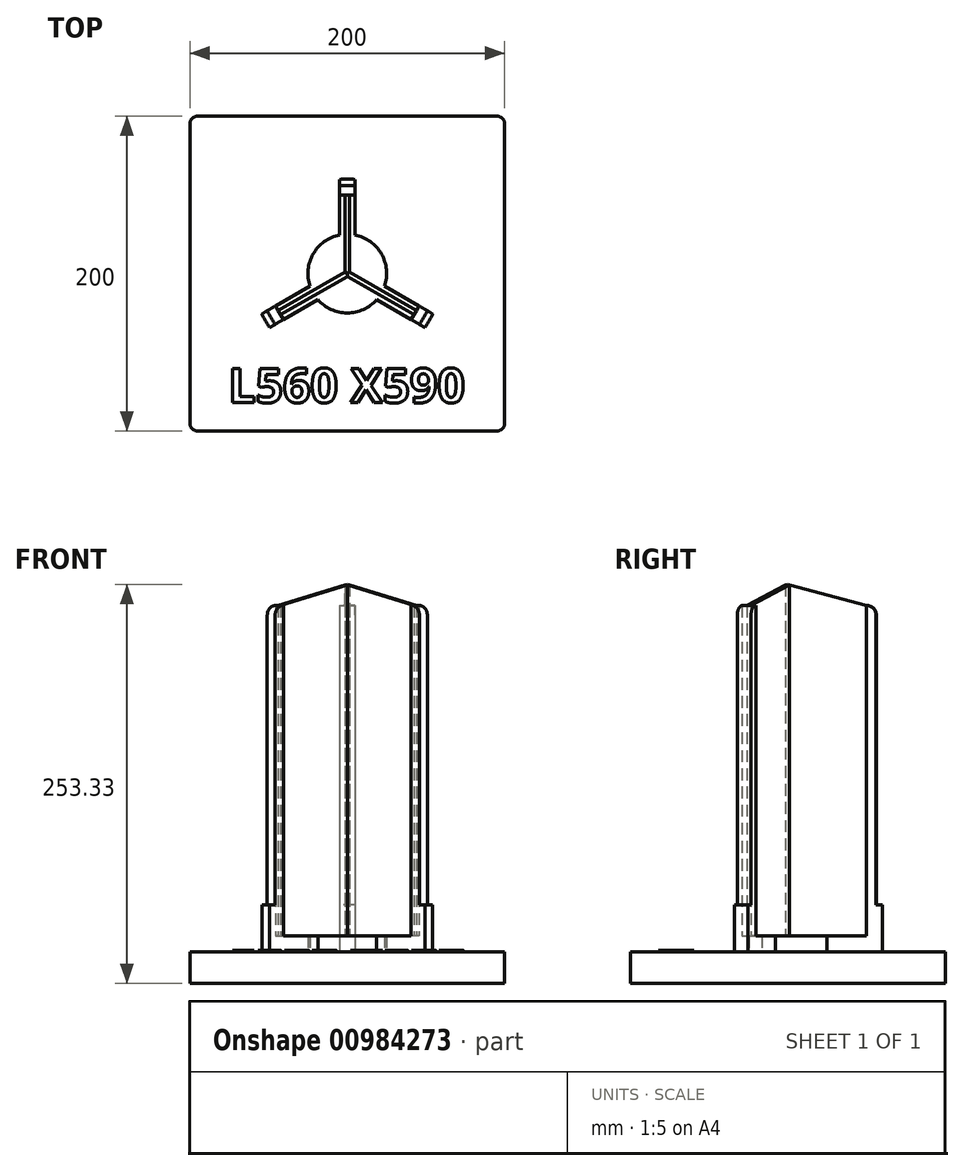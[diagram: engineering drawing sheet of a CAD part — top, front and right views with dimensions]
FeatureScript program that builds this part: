
annotation { "Feature Type Name" : "Feature", "Feature Type Description" : "" }
export const myFeature = defineFeature(function(context is Context, id is Id, definition is map)
    precondition{}
    {
        {
            var Q0;
            Q0=qCreatedBy(makeId("Top.planeOp"),FACE);
            var sketch = newSketch(context, id + "F0", { "sketchPlane" : qUnion([Q0])});
            skCircle(sketch, "E0", {"center": v(0, 0) * mm, "radius": 60 * mm});
            skCircle(sketch, "E1", {"center": v(0, 0) * mm, "radius": 56 * mm});
            skCircle(sketch, "E2", {"center": v(0, 0) * mm, "radius": 25 * mm});
            skLineSegment(sketch, "E3", {"start": v(-1.5, 55.98) * mm, "end": v(1.5, 55.98) * mm, "construction": true});
            skLineSegment(sketch, "E4", {"start": v(-5, 59.8) * mm, "end": v(5, 59.8) * mm, "construction": true});
            skCircle(sketch, "E5", {"center": v(0, 0) * mm, "radius": 1.5 * mm, "construction": true});
            skLineSegment(sketch, "E6", {"start": v(-1.5, 55.98) * mm, "end": v(-1.5, 0) * mm});
            skLineSegment(sketch, "E7", {"start": v(1.5, 55.98) * mm, "end": v(1.5, 0) * mm});
            skLineSegment(sketch, "E8", {"start": v(-5, 59.8) * mm, "end": v(-5, 55.78) * mm});
            skLineSegment(sketch, "E9", {"start": v(5, 59.8) * mm, "end": v(5, 55.78) * mm});
            skLineSegment(sketch, "E10", {"start": v(-1.5, 24.95) * mm, "end": v(-22.36, -11.18) * mm, "construction": true});
            skCircle(sketch, "E11", {"center": v(-11.93, 6.89) * mm, "radius": 3.5 * mm});
            skCircle(sketch, "E12", {"center": v(-11.93, 6.89) * mm, "radius": 1.75 * mm});
            skCircle(sketch, "E13.1.0", {"center": v(0, -13.78) * mm, "radius": 1.75 * mm});
            skCircle(sketch, "E13.1.1", {"center": v(0, -13.78) * mm, "radius": 3.5 * mm});
            skCircle(sketch, "E13.2.0", {"center": v(11.93, 6.89) * mm, "radius": 1.75 * mm});
            skCircle(sketch, "E13.2.1", {"center": v(11.93, 6.89) * mm, "radius": 3.5 * mm});
            skLineSegment(sketch, "E14", {"start": v(-5, 55.78) * mm, "end": v(-5, 24.5) * mm});
            skLineSegment(sketch, "E15", {"start": v(5, 55.78) * mm, "end": v(5, 24.5) * mm});
            skCircle(sketch, "E16", {"center": v(0, 0) * mm, "radius": 50 * mm, "construction": true});
            skLineSegment(sketch, "E17", {"start": v(-5, 49.75) * mm, "end": v(5, 49.75) * mm});
            skLineSegment(sketch, "E18.1.0", {"start": v(-47.73, -29.29) * mm, "end": v(0.75, -1.3) * mm});
            skLineSegment(sketch, "E18.1.1", {"start": v(-49.23, -26.7) * mm, "end": v(-0.75, 1.3) * mm});
            skLineSegment(sketch, "E18.1.2", {"start": v(-45.8, -32.22) * mm, "end": v(-18.71, -16.58) * mm});
            skLineSegment(sketch, "E18.1.3", {"start": v(-50.8, -23.56) * mm, "end": v(-23.71, -7.92) * mm});
            skLineSegment(sketch, "E18.1.4", {"start": v(-49.28, -34.23) * mm, "end": v(-45.8, -32.22) * mm});
            skLineSegment(sketch, "E18.1.5", {"start": v(-54.28, -25.57) * mm, "end": v(-50.8, -23.56) * mm});
            skLineSegment(sketch, "E18.1.6", {"start": v(-49.28, -34.23) * mm, "end": v(-54.28, -25.57) * mm, "construction": true});
            skLineSegment(sketch, "E18.1.7", {"start": v(-47.73, -29.29) * mm, "end": v(-49.23, -26.7) * mm, "construction": true});
            skLineSegment(sketch, "E18.1.8", {"start": v(-40.58, -29.2) * mm, "end": v(-45.58, -20.54) * mm});
            skLineSegment(sketch, "E18.2.0", {"start": v(49.23, -26.7) * mm, "end": v(0.75, 1.3) * mm});
            skLineSegment(sketch, "E18.2.1", {"start": v(47.73, -29.29) * mm, "end": v(-0.75, -1.3) * mm});
            skLineSegment(sketch, "E18.2.2", {"start": v(50.8, -23.56) * mm, "end": v(23.71, -7.92) * mm});
            skLineSegment(sketch, "E18.2.3", {"start": v(45.8, -32.22) * mm, "end": v(18.71, -16.58) * mm});
            skLineSegment(sketch, "E18.2.4", {"start": v(54.28, -25.57) * mm, "end": v(50.8, -23.56) * mm});
            skLineSegment(sketch, "E18.2.5", {"start": v(49.28, -34.23) * mm, "end": v(45.8, -32.22) * mm});
            skLineSegment(sketch, "E18.2.6", {"start": v(54.28, -25.57) * mm, "end": v(49.28, -34.23) * mm, "construction": true});
            skLineSegment(sketch, "E18.2.7", {"start": v(49.23, -26.7) * mm, "end": v(47.73, -29.29) * mm, "construction": true});
            skLineSegment(sketch, "E18.2.8", {"start": v(45.58, -20.54) * mm, "end": v(40.58, -29.2) * mm});
            skText(sketch, "E19", { "text": "L560 X590", "fontName": "OpenSans-Bold.ttf"});
            const initialGuessF0  = {"E19": [-0.07556, -0.082, 1, 0, 0.022]};
            skSetInitialGuess(sketch, initialGuessF0);
            skSolve(sketch);
        }
        {
            var Q0;
            {var subQ0=sQuery(id+"F0.wireOp",EDGE,"E2");var subQ1=sQuery(id+"F0.wireOp",EDGE,"Qz9RoNIK-bmAM-g4SH-EP3c-7Fqs6VSRPzqB.left");var subQ2=makeQuery(id+"F0.imprint","INTERSECT",VERTEX,{"disambiguationData":[OD(0.0)],"derivedFrom":[subQ1,subQ0]});Q0=makeQuery(id+"F0.imprint","IMPRINT",FACE,{"disambiguationData":[TD([[makeQuery(id+"F0.imprint","IMPRINT",EDGE,{"disambiguationData":[TD([[subQ2,-1.0]])],"derivedFrom":subQ1}),1.0]])]});}
            var Q1;
            {var subQ0=sQuery(id+"F0.wireOp",EDGE,"E2");var subQ1=sQuery(id+"F0.wireOp",EDGE,"Qz9RoNIK-bmAM-g4SH-EP3c-7Fqs6VSRPzqB.left");var subQ2=makeQuery(id+"F0.imprint","INTERSECT",VERTEX,{"disambiguationData":[OD(0.0)],"derivedFrom":[subQ1,subQ0]});Q1=makeQuery(id+"F0.imprint","IMPRINT",FACE,{"disambiguationData":[TD([[makeQuery(id+"F0.imprint","IMPRINT",EDGE,{"disambiguationData":[TD([[subQ2,-1.0]])],"derivedFrom":subQ1}),-1.0]])]});}
            var Q2;
            {var subQ1=sQuery(id+"F0.wireOp",EDGE,"Qz9RoNIK-bmAM-g4SH-EP3c-7Fqs6VSRPzqB.right");var subQ5=sQuery(id+"F0.wireOp",EDGE,"E2");var subQ6=makeQuery(id+"F0.imprint","INTERSECT",VERTEX,{"disambiguationData":[OD(0.0)],"derivedFrom":[subQ1,subQ5]});Q2=makeQuery(id+"F0.imprint","IMPRINT",FACE,{"disambiguationData":[TD([[makeQuery(id+"F0.imprint","IMPRINT",EDGE,{"disambiguationData":[TD([[subQ6,-1.0]])],"derivedFrom":subQ1}),-1.0]])]});}
            var Q3;
            {var subQ5=sQuery(id+"F0.wireOp",EDGE,"Qz9RoNIK-bmAM-g4SH-EP3c-7Fqs6VSRPzqB.right");var subQ7=sQuery(id+"F0.wireOp",EDGE,"I0Sq5aEr-Hngn-Fm4D-tp8S-rX2HjxpjUaP6.bottom");var subQ8=makeQuery(id+"F0.imprint","INTERSECT",VERTEX,{"derivedFrom":[subQ5,subQ7]});Q3=makeQuery(id+"F0.imprint","IMPRINT",FACE,{"disambiguationData":[TD([[makeQuery(id+"F0.imprint","IMPRINT",EDGE,{"disambiguationData":[TD([[subQ8,-1.0]])],"derivedFrom":subQ5}),-1.0]])]});}
            var Q4;
            {var subQ0=sQuery(id+"F0.wireOp",EDGE,"I0Sq5aEr-Hngn-Fm4D-tp8S-rX2HjxpjUaP6.bottom");var subQ1=sQuery(id+"F0.wireOp",EDGE,"Qz9RoNIK-bmAM-g4SH-EP3c-7Fqs6VSRPzqB.left");var subQ2=makeQuery(id+"F0.imprint","INTERSECT",VERTEX,{"derivedFrom":[subQ1,subQ0]});Q4=makeQuery(id+"F0.imprint","IMPRINT",FACE,{"disambiguationData":[TD([[makeQuery(id+"F0.imprint","IMPRINT",EDGE,{"disambiguationData":[TD([[subQ2,-1.0]])],"derivedFrom":subQ1}),-1.0]])]});}
            var Q5;
            {var subQ5=sQuery(id+"F0.wireOp",EDGE,"Qz9RoNIK-bmAM-g4SH-EP3c-7Fqs6VSRPzqB.left");var subQ7=sQuery(id+"F0.wireOp",EDGE,"I0Sq5aEr-Hngn-Fm4D-tp8S-rX2HjxpjUaP6.bottom");var subQ8=makeQuery(id+"F0.imprint","INTERSECT",VERTEX,{"derivedFrom":[subQ5,subQ7]});Q5=makeQuery(id+"F0.imprint","IMPRINT",FACE,{"disambiguationData":[TD([[makeQuery(id+"F0.imprint","IMPRINT",EDGE,{"disambiguationData":[TD([[subQ8,-1.0]])],"derivedFrom":subQ5}),1.0]])]});}
            var Q6;
            {var subQ0=sQuery(id+"F0.wireOp",EDGE,"MHhcaKt2-idaq-ussF-yxv1-Ysw6X7YejIML.top");var subQ1=sQuery(id+"F0.wireOp",EDGE,"Qz9RoNIK-bmAM-g4SH-EP3c-7Fqs6VSRPzqB.left");var subQ2=makeQuery(id+"F0.imprint","INTERSECT",VERTEX,{"derivedFrom":[subQ1,subQ0]});Q6=makeQuery(id+"F0.imprint","IMPRINT",FACE,{"disambiguationData":[TD([[makeQuery(id+"F0.imprint","IMPRINT",EDGE,{"disambiguationData":[TD([[subQ2,-1.0]])],"derivedFrom":subQ1}),1.0]])]});}
            var Q7;
            {var subQ0=sQuery(id+"F0.wireOp",EDGE,"MHhcaKt2-idaq-ussF-yxv1-Ysw6X7YejIML.top");var subQ1=sQuery(id+"F0.wireOp",EDGE,"Qz9RoNIK-bmAM-g4SH-EP3c-7Fqs6VSRPzqB.left");var subQ2=makeQuery(id+"F0.imprint","INTERSECT",VERTEX,{"derivedFrom":[subQ1,subQ0]});Q7=makeQuery(id+"F0.imprint","IMPRINT",FACE,{"disambiguationData":[TD([[makeQuery(id+"F0.imprint","IMPRINT",EDGE,{"disambiguationData":[TD([[subQ2,-1.0]])],"derivedFrom":subQ1}),-1.0]])]});}
            var Q8;
            {var subQ0=sQuery(id+"F0.wireOp",EDGE,"MHhcaKt2-idaq-ussF-yxv1-Ysw6X7YejIML.top");var subQ1=sQuery(id+"F0.wireOp",EDGE,"Qz9RoNIK-bmAM-g4SH-EP3c-7Fqs6VSRPzqB.right");var subQ2=makeQuery(id+"F0.imprint","INTERSECT",VERTEX,{"derivedFrom":[subQ1,subQ0]});Q8=makeQuery(id+"F0.imprint","IMPRINT",FACE,{"disambiguationData":[TD([[makeQuery(id+"F0.imprint","IMPRINT",EDGE,{"disambiguationData":[TD([[subQ2,-1.0]])],"derivedFrom":subQ1}),-1.0]])]});}
            var Q9;
            {var subQ0=sQuery(id+"F0.wireOp",EDGE,"I0Sq5aEr-Hngn-Fm4D-tp8S-rX2HjxpjUaP6.right");var subQ1=sQuery(id+"F0.wireOp",EDGE,"MHhcaKt2-idaq-ussF-yxv1-Ysw6X7YejIML.bottom");var subQ2=makeQuery(id+"F0.imprint","INTERSECT",VERTEX,{"derivedFrom":[subQ1,subQ0]});Q9=makeQuery(id+"F0.imprint","IMPRINT",FACE,{"disambiguationData":[TD([[makeQuery(id+"F0.imprint","IMPRINT",EDGE,{"disambiguationData":[TD([[subQ2,-1.0]])],"derivedFrom":subQ1}),-1.0]])]});}
            var Q10;
            {var subQ0=sQuery(id+"F0.wireOp",EDGE,"I0Sq5aEr-Hngn-Fm4D-tp8S-rX2HjxpjUaP6.top");var subQ1=sQuery(id+"F0.wireOp",EDGE,"Qz9RoNIK-bmAM-g4SH-EP3c-7Fqs6VSRPzqB.right");var subQ2=makeQuery(id+"F0.imprint","INTERSECT",VERTEX,{"derivedFrom":[subQ1,subQ0]});Q10=makeQuery(id+"F0.imprint","IMPRINT",FACE,{"disambiguationData":[TD([[makeQuery(id+"F0.imprint","IMPRINT",EDGE,{"disambiguationData":[TD([[subQ2,-1.0]])],"derivedFrom":subQ1}),-1.0]])]});}
            var Q11;
            {var subQ1=sQuery(id+"F0.wireOp",EDGE,"MHhcaKt2-idaq-ussF-yxv1-Ysw6X7YejIML.bottom");var subQ7=sQuery(id+"F0.wireOp",EDGE,"Qz9RoNIK-bmAM-g4SH-EP3c-7Fqs6VSRPzqB.right");var subQ8=makeQuery(id+"F0.imprint","INTERSECT",VERTEX,{"derivedFrom":[subQ7,subQ1]});Q11=makeQuery(id+"F0.imprint","IMPRINT",FACE,{"disambiguationData":[TD([[makeQuery(id+"F0.imprint","IMPRINT",EDGE,{"disambiguationData":[TD([[subQ8,-1.0]])],"derivedFrom":subQ7}),-1.0]])]});}
            var Q12;
            {var subQ0=sQuery(id+"F0.wireOp",EDGE,"MHhcaKt2-idaq-ussF-yxv1-Ysw6X7YejIML.bottom");var subQ1=sQuery(id+"F0.wireOp",EDGE,"Qz9RoNIK-bmAM-g4SH-EP3c-7Fqs6VSRPzqB.left");var subQ2=makeQuery(id+"F0.imprint","INTERSECT",VERTEX,{"derivedFrom":[subQ1,subQ0]});Q12=makeQuery(id+"F0.imprint","IMPRINT",FACE,{"disambiguationData":[TD([[makeQuery(id+"F0.imprint","IMPRINT",EDGE,{"disambiguationData":[TD([[subQ2,-1.0]])],"derivedFrom":subQ1}),-1.0]])]});}
            var Q13;
            {var subQ1=sQuery(id+"F0.wireOp",EDGE,"MHhcaKt2-idaq-ussF-yxv1-Ysw6X7YejIML.bottom");var subQ7=sQuery(id+"F0.wireOp",EDGE,"Qz9RoNIK-bmAM-g4SH-EP3c-7Fqs6VSRPzqB.left");var subQ8=makeQuery(id+"F0.imprint","INTERSECT",VERTEX,{"derivedFrom":[subQ7,subQ1]});Q13=makeQuery(id+"F0.imprint","IMPRINT",FACE,{"disambiguationData":[TD([[makeQuery(id+"F0.imprint","IMPRINT",EDGE,{"disambiguationData":[TD([[subQ8,-1.0]])],"derivedFrom":subQ7}),1.0]])]});}
            var Q14;
            {var subQ0=sQuery(id+"F0.wireOp",EDGE,"I0Sq5aEr-Hngn-Fm4D-tp8S-rX2HjxpjUaP6.top");var subQ1=sQuery(id+"F0.wireOp",EDGE,"Qz9RoNIK-bmAM-g4SH-EP3c-7Fqs6VSRPzqB.left");var subQ2=makeQuery(id+"F0.imprint","INTERSECT",VERTEX,{"derivedFrom":[subQ1,subQ0]});Q14=makeQuery(id+"F0.imprint","IMPRINT",FACE,{"disambiguationData":[TD([[makeQuery(id+"F0.imprint","IMPRINT",EDGE,{"disambiguationData":[TD([[subQ2,-1.0]])],"derivedFrom":subQ1}),1.0]])]});}
            var Q15;
            {var subQ0=sQuery(id+"F0.wireOp",EDGE,"E2");var subQ1=sQuery(id+"F0.wireOp",EDGE,"MHhcaKt2-idaq-ussF-yxv1-Ysw6X7YejIML.bottom");var subQ2=makeQuery(id+"F0.imprint","INTERSECT",VERTEX,{"disambiguationData":[OD(0.0)],"derivedFrom":[subQ1,subQ0]});Q15=makeQuery(id+"F0.imprint","IMPRINT",FACE,{"disambiguationData":[TD([[makeQuery(id+"F0.imprint","IMPRINT",EDGE,{"disambiguationData":[TD([[subQ2,-1.0]])],"derivedFrom":subQ1}),-1.0]])]});}
            var Q16;
            {var subQ0=sQuery(id+"F0.wireOp",EDGE,"I0Sq5aEr-Hngn-Fm4D-tp8S-rX2HjxpjUaP6.top");var subQ1=sQuery(id+"F0.wireOp",EDGE,"Qz9RoNIK-bmAM-g4SH-EP3c-7Fqs6VSRPzqB.left");var subQ2=makeQuery(id+"F0.imprint","INTERSECT",VERTEX,{"derivedFrom":[subQ1,subQ0]});Q16=makeQuery(id+"F0.imprint","IMPRINT",FACE,{"disambiguationData":[TD([[makeQuery(id+"F0.imprint","IMPRINT",EDGE,{"disambiguationData":[TD([[subQ2,-1.0]])],"derivedFrom":subQ1}),-1.0]])]});}
            var Q17;
            {var subQ0=sQuery(id+"F0.wireOp",EDGE,"ARnEnpE5-tkmW-Q9Fp-N7HQ-ZdpaRJQSmeqH.top");Q17=makeQuery(id+"F0.imprint","IMPRINT",FACE,{"disambiguationData":[TD([[makeQuery(id+"F0.imprint","IMPRINT",EDGE,{"derivedFrom":subQ0}),1.0]])]});}
            var Q18;
            {var subQ0=sQuery(id+"F0.wireOp",EDGE,"fYTYB3PY-5dvC-i0FG-IhBz-imLdNv0oFj73.right");Q18=makeQuery(id+"F0.imprint","IMPRINT",FACE,{"disambiguationData":[TD([[makeQuery(id+"F0.imprint","IMPRINT",EDGE,{"derivedFrom":subQ0}),-1.0]])]});}
            var Q19;
            {var subQ0=sQuery(id+"F0.wireOp",EDGE,"JRACFuVa-LFQl-MoOF-o5kD-FoGYgOgg0vGQ.top");Q19=makeQuery(id+"F0.imprint","IMPRINT",FACE,{"disambiguationData":[TD([[makeQuery(id+"F0.imprint","IMPRINT",EDGE,{"derivedFrom":subQ0}),-1.0]])]});}
            var Q20;
            {var subQ0=sQuery(id+"F0.wireOp",EDGE,"qvxIDn41-u5vC-3tcf-A1ba-gfAf9TCSAjBw.right");Q20=makeQuery(id+"F0.imprint","IMPRINT",FACE,{"disambiguationData":[TD([[makeQuery(id+"F0.imprint","IMPRINT",EDGE,{"derivedFrom":subQ0}),1.0]])]});}
            var Q21;
            {var subQ0=sQuery(id+"F0.wireOp",EDGE,"E2");var subQ1=sQuery(id+"F0.wireOp",EDGE,"Qz9RoNIK-bmAM-g4SH-EP3c-7Fqs6VSRPzqB.right");var subQ2=makeQuery(id+"F0.imprint","INTERSECT",VERTEX,{"disambiguationData":[OD(0.0)],"derivedFrom":[subQ1,subQ0]});Q21=makeQuery(id+"F0.imprint","IMPRINT",FACE,{"disambiguationData":[TD([[makeQuery(id+"F0.imprint","IMPRINT",EDGE,{"disambiguationData":[TD([[subQ2,-1.0]])],"derivedFrom":subQ1}),1.0]])]});}
            var Q22;
            {var subQ0=sQuery(id+"F0.wireOp",EDGE,"I0Sq5aEr-Hngn-Fm4D-tp8S-rX2HjxpjUaP6.bottom");var subQ1=sQuery(id+"F0.wireOp",EDGE,"Qz9RoNIK-bmAM-g4SH-EP3c-7Fqs6VSRPzqB.right");var subQ2=makeQuery(id+"F0.imprint","INTERSECT",VERTEX,{"derivedFrom":[subQ1,subQ0]});Q22=makeQuery(id+"F0.imprint","IMPRINT",FACE,{"disambiguationData":[TD([[makeQuery(id+"F0.imprint","IMPRINT",EDGE,{"disambiguationData":[TD([[subQ2,-1.0]])],"derivedFrom":subQ1}),1.0]])]});}
            var Q23;
            {var subQ0=sQuery(id+"F0.wireOp",EDGE,"MHhcaKt2-idaq-ussF-yxv1-Ysw6X7YejIML.top");var subQ1=sQuery(id+"F0.wireOp",EDGE,"Qz9RoNIK-bmAM-g4SH-EP3c-7Fqs6VSRPzqB.right");var subQ2=makeQuery(id+"F0.imprint","INTERSECT",VERTEX,{"derivedFrom":[subQ1,subQ0]});Q23=makeQuery(id+"F0.imprint","IMPRINT",FACE,{"disambiguationData":[TD([[makeQuery(id+"F0.imprint","IMPRINT",EDGE,{"disambiguationData":[TD([[subQ2,-1.0]])],"derivedFrom":subQ1}),1.0]])]});}
            var Q24;
            {var subQ0=sQuery(id+"F0.wireOp",EDGE,"I0Sq5aEr-Hngn-Fm4D-tp8S-rX2HjxpjUaP6.right");var subQ1=sQuery(id+"F0.wireOp",EDGE,"MHhcaKt2-idaq-ussF-yxv1-Ysw6X7YejIML.top");var subQ2=makeQuery(id+"F0.imprint","INTERSECT",VERTEX,{"derivedFrom":[subQ1,subQ0]});Q24=makeQuery(id+"F0.imprint","IMPRINT",FACE,{"disambiguationData":[TD([[makeQuery(id+"F0.imprint","IMPRINT",EDGE,{"disambiguationData":[TD([[subQ2,-1.0]])],"derivedFrom":subQ1}),1.0]])]});}
            var Q25;
            {var subQ0=sQuery(id+"F0.wireOp",EDGE,"MHhcaKt2-idaq-ussF-yxv1-Ysw6X7YejIML.bottom");var subQ1=sQuery(id+"F0.wireOp",EDGE,"Qz9RoNIK-bmAM-g4SH-EP3c-7Fqs6VSRPzqB.right");var subQ2=makeQuery(id+"F0.imprint","INTERSECT",VERTEX,{"derivedFrom":[subQ1,subQ0]});Q25=makeQuery(id+"F0.imprint","IMPRINT",FACE,{"disambiguationData":[TD([[makeQuery(id+"F0.imprint","IMPRINT",EDGE,{"disambiguationData":[TD([[subQ2,-1.0]])],"derivedFrom":subQ1}),1.0]])]});}
            var Q26;
            {var subQ0=sQuery(id+"F0.wireOp",EDGE,"I0Sq5aEr-Hngn-Fm4D-tp8S-rX2HjxpjUaP6.top");var subQ1=sQuery(id+"F0.wireOp",EDGE,"Qz9RoNIK-bmAM-g4SH-EP3c-7Fqs6VSRPzqB.right");var subQ2=makeQuery(id+"F0.imprint","INTERSECT",VERTEX,{"derivedFrom":[subQ1,subQ0]});Q26=makeQuery(id+"F0.imprint","IMPRINT",FACE,{"disambiguationData":[TD([[makeQuery(id+"F0.imprint","IMPRINT",EDGE,{"disambiguationData":[TD([[subQ2,-1.0]])],"derivedFrom":subQ1}),1.0]])]});}
            var Q27;
            {var subQ0=sQuery(id+"F0.wireOp",EDGE,"UooLEnTI-Uf4f-MH2r-6JwD-Mf36DO2BtYOc.top");var subQ1=sQuery(id+"F0.wireOp",EDGE,"Qz9RoNIK-bmAM-g4SH-EP3c-7Fqs6VSRPzqB.right");var subQ2=makeQuery(id+"F0.imprint","INTERSECT",VERTEX,{"derivedFrom":[subQ1,subQ0]});Q27=makeQuery(id+"F0.imprint","IMPRINT",FACE,{"disambiguationData":[TD([[makeQuery(id+"F0.imprint","IMPRINT",EDGE,{"disambiguationData":[TD([[subQ2,-1.0]])],"derivedFrom":subQ1}),-1.0]])]});}
            var Q28;
            {var subQ0=sQuery(id+"F0.wireOp",EDGE,"UooLEnTI-Uf4f-MH2r-6JwD-Mf36DO2BtYOc.top");var subQ1=sQuery(id+"F0.wireOp",EDGE,"Qz9RoNIK-bmAM-g4SH-EP3c-7Fqs6VSRPzqB.right");var subQ2=makeQuery(id+"F0.imprint","INTERSECT",VERTEX,{"derivedFrom":[subQ1,subQ0]});Q28=makeQuery(id+"F0.imprint","IMPRINT",FACE,{"disambiguationData":[TD([[makeQuery(id+"F0.imprint","IMPRINT",EDGE,{"disambiguationData":[TD([[subQ2,-1.0]])],"derivedFrom":subQ1}),1.0]])]});}
            var Q29;
            {var subQ0=sQuery(id+"F0.wireOp",EDGE,"UooLEnTI-Uf4f-MH2r-6JwD-Mf36DO2BtYOc.top");var subQ1=sQuery(id+"F0.wireOp",EDGE,"Qz9RoNIK-bmAM-g4SH-EP3c-7Fqs6VSRPzqB.left");var subQ2=makeQuery(id+"F0.imprint","INTERSECT",VERTEX,{"derivedFrom":[subQ1,subQ0]});Q29=makeQuery(id+"F0.imprint","IMPRINT",FACE,{"disambiguationData":[TD([[makeQuery(id+"F0.imprint","IMPRINT",EDGE,{"disambiguationData":[TD([[subQ2,-1.0]])],"derivedFrom":subQ1}),-1.0]])]});}
            var Q30;
            {var subQ0=sQuery(id+"F0.wireOp",EDGE,"UooLEnTI-Uf4f-MH2r-6JwD-Mf36DO2BtYOc.top");var subQ1=sQuery(id+"F0.wireOp",EDGE,"Qz9RoNIK-bmAM-g4SH-EP3c-7Fqs6VSRPzqB.left");var subQ2=makeQuery(id+"F0.imprint","INTERSECT",VERTEX,{"derivedFrom":[subQ1,subQ0]});Q30=makeQuery(id+"F0.imprint","IMPRINT",FACE,{"disambiguationData":[TD([[makeQuery(id+"F0.imprint","IMPRINT",EDGE,{"disambiguationData":[TD([[subQ2,-1.0]])],"derivedFrom":subQ1}),1.0]])]});}
            var Q31;
            {var subQ0=sQuery(id+"F0.wireOp",EDGE,"E2");var subQ1=sQuery(id+"F0.wireOp",EDGE,"MHhcaKt2-idaq-ussF-yxv1-Ysw6X7YejIML.top");var subQ2=makeQuery(id+"F0.imprint","INTERSECT",VERTEX,{"disambiguationData":[OD(0.0)],"derivedFrom":[subQ1,subQ0]});Q31=makeQuery(id+"F0.imprint","IMPRINT",FACE,{"disambiguationData":[TD([[makeQuery(id+"F0.imprint","IMPRINT",EDGE,{"disambiguationData":[TD([[subQ2,-1.0]])],"derivedFrom":subQ1}),1.0]])]});}
            var Q32;
            {var subQ0=sQuery(id+"F0.wireOp",EDGE,"UaoCu7b1-m9SB-61mE-joAU-4Tf4ClvXxRAN");var subQ4=sQuery(id+"F0.wireOp",EDGE,"Z93t4qtu-qqve-2JoU-aCnr-fMp0EEGuzRtp");var subQ5=makeQuery(id+"F0.imprint","INTERSECT",VERTEX,{"disambiguationData":[OD(0.0)],"derivedFrom":[subQ4,subQ0]});Q32=makeQuery(id+"F0.imprint","IMPRINT",FACE,{"disambiguationData":[TD([[makeQuery(id+"F0.imprint","IMPRINT",EDGE,{"disambiguationData":[TD([[subQ5,1.0]])],"derivedFrom":subQ4}),-1.0]])]});}
            var Q33;
            Q33=makeQuery(id+"F0.imprint","IMPRINT",FACE,{"disambiguationData":[TD([[makeQuery(id+"F0.imprint","IMPRINT",EDGE,{"derivedFrom":sQuery(id+"F0.wireOp",EDGE,"3ba069c8-a511-4e33-be52-923c701046d1.1.1")}),-1.0]])]});
            var Q34;
            {var subQ5=sQuery(id+"F0.wireOp",EDGE,"3ec345ef-f0f0-4e93-9e5e-b6a35eb55933.1.2");var subQ6=sQuery(id+"F0.wireOp",EDGE,"E2");var subQ7=makeQuery(id+"F0.imprint","INTERSECT",VERTEX,{"derivedFrom":[subQ6,subQ5]});Q34=makeQuery(id+"F0.imprint","IMPRINT",FACE,{"disambiguationData":[TD([[makeQuery(id+"F0.imprint","IMPRINT",EDGE,{"disambiguationData":[TD([[subQ7,-1.0]])],"derivedFrom":subQ6}),1.0]])]});}
            var Q35;
            {var subQ1=sQuery(id+"F0.wireOp",EDGE,"E2");var subQ7=sQuery(id+"F0.wireOp",EDGE,"3ec345ef-f0f0-4e93-9e5e-b6a35eb55933.2.6");var subQ9=makeQuery(id+"F0.imprint","INTERSECT",VERTEX,{"derivedFrom":[subQ1,subQ7]});Q35=makeQuery(id+"F0.imprint","IMPRINT",FACE,{"disambiguationData":[TD([[makeQuery(id+"F0.imprint","IMPRINT",EDGE,{"disambiguationData":[TD([[subQ9,-1.0]])],"derivedFrom":subQ1}),1.0]])]});}
            var Q36;
            {var subQ1=sQuery(id+"F0.wireOp",EDGE,"Qz9RoNIK-bmAM-g4SH-EP3c-7Fqs6VSRPzqB.left");var subQ5=sQuery(id+"F0.wireOp",EDGE,"Fhyrr48q-6Ub6-qUJE-WvSH-lKAYv9wGpefs");var subQ6=makeQuery(id+"F0.imprint","INTERSECT",VERTEX,{"derivedFrom":[subQ1,subQ5]});Q36=makeQuery(id+"F0.imprint","IMPRINT",FACE,{"disambiguationData":[TD([[makeQuery(id+"F0.imprint","IMPRINT",EDGE,{"disambiguationData":[TD([[subQ6,1.0]])],"derivedFrom":subQ1}),1.0]])]});}
            var Q37;
            {var subQ0=sQuery(id+"F0.wireOp",EDGE,"Fhyrr48q-6Ub6-qUJE-WvSH-lKAYv9wGpefs");var subQ1=sQuery(id+"F0.wireOp",EDGE,"Qz9RoNIK-bmAM-g4SH-EP3c-7Fqs6VSRPzqB.left");var subQ2=makeQuery(id+"F0.imprint","INTERSECT",VERTEX,{"derivedFrom":[subQ1,subQ0]});Q37=makeQuery(id+"F0.imprint","IMPRINT",FACE,{"disambiguationData":[TD([[makeQuery(id+"F0.imprint","IMPRINT",EDGE,{"disambiguationData":[TD([[subQ2,1.0]])],"derivedFrom":subQ1}),-1.0]])]});}
            var Q38;
            {var subQ3=sQuery(id+"F0.wireOp",EDGE,"3ec345ef-f0f0-4e93-9e5e-b6a35eb55933.1.15");var subQ7=sQuery(id+"F0.wireOp",EDGE,"3ec345ef-f0f0-4e93-9e5e-b6a35eb55933.1.0");var subQ8=makeQuery(id+"F0.imprint","INTERSECT",VERTEX,{"derivedFrom":[subQ7,subQ3]});Q38=makeQuery(id+"F0.imprint","IMPRINT",FACE,{"disambiguationData":[TD([[makeQuery(id+"F0.imprint","IMPRINT",EDGE,{"disambiguationData":[TD([[subQ8,1.0]])],"derivedFrom":subQ7}),1.0]])]});}
            var Q39;
            {var subQ0=sQuery(id+"F0.wireOp",EDGE,"15ffb876-a102-4fbe-8a3e-136bf1afb38e.1.1");Q39=makeQuery(id+"F0.imprint","IMPRINT",FACE,{"disambiguationData":[TD([[makeQuery(id+"F0.imprint","IMPRINT",EDGE,{"derivedFrom":subQ0}),-1.0]])]});}
            var Q40;
            {var subQ3=sQuery(id+"F0.wireOp",EDGE,"15ffb876-a102-4fbe-8a3e-136bf1afb38e.1.4");Q40=makeQuery(id+"F0.imprint","IMPRINT",FACE,{"disambiguationData":[TD([[makeQuery(id+"F0.imprint","IMPRINT",EDGE,{"derivedFrom":subQ3}),1.0]])]});}
            var Q41;
            {var subQ0=sQuery(id+"F0.wireOp",EDGE,"15ffb876-a102-4fbe-8a3e-136bf1afb38e.2.1");Q41=makeQuery(id+"F0.imprint","IMPRINT",FACE,{"disambiguationData":[TD([[makeQuery(id+"F0.imprint","IMPRINT",EDGE,{"derivedFrom":subQ0}),-1.0]])]});}
            var Q42;
            {var subQ3=sQuery(id+"F0.wireOp",EDGE,"15ffb876-a102-4fbe-8a3e-136bf1afb38e.2.4");Q42=makeQuery(id+"F0.imprint","IMPRINT",FACE,{"disambiguationData":[TD([[makeQuery(id+"F0.imprint","IMPRINT",EDGE,{"derivedFrom":subQ3}),1.0]])]});}
            var Q43;
            {var subQ0=sQuery(id+"F0.wireOp",EDGE,"E18.1.3");var subQ1=sQuery(id+"F0.wireOp",EDGE,"E2");var subQ2=makeQuery(id+"F0.imprint","INTERSECT",VERTEX,{"derivedFrom":[subQ1,subQ0]});Q43=makeQuery(id+"F0.imprint","IMPRINT",FACE,{"disambiguationData":[TD([[makeQuery(id+"F0.imprint","IMPRINT",EDGE,{"disambiguationData":[TD([[subQ2,-1.0]])],"derivedFrom":subQ1}),-1.0]])]});}
            var Q44;
            {var subQ0=sQuery(id+"F0.wireOp",EDGE,"E18.1.2");var subQ1=sQuery(id+"F0.wireOp",EDGE,"E2");var subQ2=makeQuery(id+"F0.imprint","INTERSECT",VERTEX,{"derivedFrom":[subQ1,subQ0]});Q44=makeQuery(id+"F0.imprint","IMPRINT",FACE,{"disambiguationData":[TD([[makeQuery(id+"F0.imprint","IMPRINT",EDGE,{"disambiguationData":[TD([[subQ2,1.0]])],"derivedFrom":subQ1}),-1.0]])]});}
            var Q45;
            {var subQ0=sQuery(id+"F0.wireOp",EDGE,"E18.2.3");var subQ1=sQuery(id+"F0.wireOp",EDGE,"E2");var subQ2=makeQuery(id+"F0.imprint","INTERSECT",VERTEX,{"derivedFrom":[subQ1,subQ0]});Q45=makeQuery(id+"F0.imprint","IMPRINT",FACE,{"disambiguationData":[TD([[makeQuery(id+"F0.imprint","IMPRINT",EDGE,{"disambiguationData":[TD([[subQ2,-1.0]])],"derivedFrom":subQ1}),-1.0]])]});}
            var Q46;
            {var subQ0=sQuery(id+"F0.wireOp",EDGE,"E18.2.2");var subQ1=sQuery(id+"F0.wireOp",EDGE,"E2");var subQ2=makeQuery(id+"F0.imprint","INTERSECT",VERTEX,{"derivedFrom":[subQ1,subQ0]});Q46=makeQuery(id+"F0.imprint","IMPRINT",FACE,{"disambiguationData":[TD([[makeQuery(id+"F0.imprint","IMPRINT",EDGE,{"disambiguationData":[TD([[subQ2,1.0]])],"derivedFrom":subQ1}),-1.0]])]});}
            var Q47;
            {var subQ0=sQuery(id+"F0.wireOp",EDGE,"E14");var subQ1=sQuery(id+"F0.wireOp",EDGE,"E2");var subQ2=makeQuery(id+"F0.imprint","INTERSECT",VERTEX,{"derivedFrom":[subQ1,subQ0]});Q47=makeQuery(id+"F0.imprint","IMPRINT",FACE,{"disambiguationData":[TD([[makeQuery(id+"F0.imprint","IMPRINT",EDGE,{"disambiguationData":[TD([[subQ2,1.0]])],"derivedFrom":subQ1}),-1.0]])]});}
            var Q48;
            {var subQ0=sQuery(id+"F0.wireOp",EDGE,"E15");var subQ1=sQuery(id+"F0.wireOp",EDGE,"E2");var subQ2=makeQuery(id+"F0.imprint","INTERSECT",VERTEX,{"derivedFrom":[subQ1,subQ0]});Q48=makeQuery(id+"F0.imprint","IMPRINT",FACE,{"disambiguationData":[TD([[makeQuery(id+"F0.imprint","IMPRINT",EDGE,{"disambiguationData":[TD([[subQ2,-1.0]])],"derivedFrom":subQ1}),-1.0]])]});}
            var Q49;
            Q49=makeQuery(id+"F0.imprint","IMPRINT",FACE,{"disambiguationData":[TD([[makeQuery(id+"F0.imprint","IMPRINT",EDGE,{"derivedFrom":sQuery(id+"F0.wireOp",EDGE,"E11")}),1.0]])]});
            var Q50;
            Q50=makeQuery(id+"F0.imprint","IMPRINT",FACE,{"disambiguationData":[TD([[makeQuery(id+"F0.imprint","IMPRINT",EDGE,{"derivedFrom":sQuery(id+"F0.wireOp",EDGE,"E12")}),1.0]])]});
            var Q51;
            Q51=makeQuery(id+"F0.imprint","IMPRINT",FACE,{"disambiguationData":[TD([[makeQuery(id+"F0.imprint","IMPRINT",EDGE,{"derivedFrom":sQuery(id+"F0.wireOp",EDGE,"E13.2.0")}),-1.0]])]});
            var Q52;
            Q52=makeQuery(id+"F0.imprint","IMPRINT",FACE,{"disambiguationData":[TD([[makeQuery(id+"F0.imprint","IMPRINT",EDGE,{"derivedFrom":sQuery(id+"F0.wireOp",EDGE,"E13.1.0")}),-1.0]])]});
            var Q53;
            Q53=makeQuery(id+"F0.imprint","IMPRINT",FACE,{"disambiguationData":[TD([[makeQuery(id+"F0.imprint","IMPRINT",EDGE,{"derivedFrom":sQuery(id+"F0.wireOp",EDGE,"E13.1.0")}),1.0]])]});
            var Q54;
            Q54=makeQuery(id+"F0.imprint","IMPRINT",FACE,{"disambiguationData":[TD([[makeQuery(id+"F0.imprint","IMPRINT",EDGE,{"derivedFrom":sQuery(id+"F0.wireOp",EDGE,"E13.2.0")}),1.0]])]});
            extrude(context, id + "F1", {"entities" : qUnion([Q0, Q1, Q2, Q3, Q4, Q5, Q6, Q7, Q8, Q9, Q10, Q11, Q12, Q13, Q14, Q15, Q16, Q17, Q18, Q19, Q20, Q21, Q22, Q23, Q24, Q25, Q26, Q27, Q28, Q29, Q30, Q31, Q32, Q33, Q34, Q35, Q36, Q37, Q38, Q39, Q40, Q41, Q42, Q43, Q44, Q45, Q46, Q47, Q48, Q49, Q50, Q51, Q52, Q53, Q54]), "depth" : 10 * mm, "offsetDistance" : 25 * mm});
        }
        {
            var Q0;
            {var subQ0=sQuery(id+"F0.wireOp",EDGE,"E7");var subQ1=sQuery(id+"F0.wireOp",EDGE,"E1");var subQ2=makeQuery(id+"F0.imprint","INTERSECT",VERTEX,{"derivedFrom":[subQ1,subQ0]});Q0=makeQuery(id+"F0.imprint","IMPRINT",FACE,{"disambiguationData":[TD([[makeQuery(id+"F0.imprint","IMPRINT",EDGE,{"disambiguationData":[TD([[subQ2,-1.0]])],"derivedFrom":subQ0}),1.0]])]});}
            var Q1;
            {var subQ0=sQuery(id+"F0.wireOp",EDGE,"E6");var subQ1=sQuery(id+"F0.wireOp",EDGE,"E1");var subQ2=makeQuery(id+"F0.imprint","INTERSECT",VERTEX,{"derivedFrom":[subQ1,subQ0]});Q1=makeQuery(id+"F0.imprint","IMPRINT",FACE,{"disambiguationData":[TD([[makeQuery(id+"F0.imprint","IMPRINT",EDGE,{"disambiguationData":[TD([[subQ2,-1.0]])],"derivedFrom":subQ0}),-1.0]])]});}
            var Q2;
            {var subQ0=sQuery(id+"F0.wireOp",EDGE,"E18.1.0");var subQ1=sQuery(id+"F0.wireOp",EDGE,"E1");var subQ2=makeQuery(id+"F0.imprint","INTERSECT",VERTEX,{"derivedFrom":[subQ1,subQ0]});Q2=makeQuery(id+"F0.imprint","IMPRINT",FACE,{"disambiguationData":[TD([[makeQuery(id+"F0.imprint","IMPRINT",EDGE,{"disambiguationData":[TD([[subQ2,-1.0]])],"derivedFrom":subQ0}),-1.0]])]});}
            var Q3;
            {var subQ0=sQuery(id+"F0.wireOp",EDGE,"E18.1.1");var subQ1=sQuery(id+"F0.wireOp",EDGE,"E1");var subQ2=makeQuery(id+"F0.imprint","INTERSECT",VERTEX,{"derivedFrom":[subQ1,subQ0]});Q3=makeQuery(id+"F0.imprint","IMPRINT",FACE,{"disambiguationData":[TD([[makeQuery(id+"F0.imprint","IMPRINT",EDGE,{"disambiguationData":[TD([[subQ2,-1.0]])],"derivedFrom":subQ0}),1.0]])]});}
            var Q4;
            {var subQ0=sQuery(id+"F0.wireOp",EDGE,"E18.2.1");var subQ1=sQuery(id+"F0.wireOp",EDGE,"E1");var subQ2=makeQuery(id+"F0.imprint","INTERSECT",VERTEX,{"derivedFrom":[subQ1,subQ0]});Q4=makeQuery(id+"F0.imprint","IMPRINT",FACE,{"disambiguationData":[TD([[makeQuery(id+"F0.imprint","IMPRINT",EDGE,{"disambiguationData":[TD([[subQ2,-1.0]])],"derivedFrom":subQ0}),1.0]])]});}
            var Q5;
            {var subQ0=sQuery(id+"F0.wireOp",EDGE,"E18.2.0");var subQ1=sQuery(id+"F0.wireOp",EDGE,"E1");var subQ2=makeQuery(id+"F0.imprint","INTERSECT",VERTEX,{"derivedFrom":[subQ1,subQ0]});Q5=makeQuery(id+"F0.imprint","IMPRINT",FACE,{"disambiguationData":[TD([[makeQuery(id+"F0.imprint","IMPRINT",EDGE,{"disambiguationData":[TD([[subQ2,-1.0]])],"derivedFrom":subQ0}),-1.0]])]});}
            var Q6;
            {var subQ0=sQuery(id+"F0.wireOp",EDGE,"E18.1.0");var subQ1=sQuery(id+"F0.wireOp",EDGE,"E1");var subQ2=makeQuery(id+"F0.imprint","INTERSECT",VERTEX,{"derivedFrom":[subQ1,subQ0]});Q6=makeQuery(id+"F0.imprint","IMPRINT",FACE,{"disambiguationData":[TD([[makeQuery(id+"F0.imprint","IMPRINT",EDGE,{"disambiguationData":[TD([[subQ2,1.0]])],"derivedFrom":subQ1}),1.0]])]});}
            var Q7;
            {var subQ0=sQuery(id+"F0.wireOp",EDGE,"E18.2.0");var subQ1=sQuery(id+"F0.wireOp",EDGE,"E1");var subQ2=makeQuery(id+"F0.imprint","INTERSECT",VERTEX,{"derivedFrom":[subQ1,subQ0]});Q7=makeQuery(id+"F0.imprint","IMPRINT",FACE,{"disambiguationData":[TD([[makeQuery(id+"F0.imprint","IMPRINT",EDGE,{"disambiguationData":[TD([[subQ2,1.0]])],"derivedFrom":subQ1}),1.0]])]});}
            var Q8;
            {var subQ0=sQuery(id+"F0.wireOp",EDGE,"E6");var subQ1=sQuery(id+"F0.wireOp",EDGE,"E1");var subQ2=makeQuery(id+"F0.imprint","INTERSECT",VERTEX,{"derivedFrom":[subQ1,subQ0]});Q8=makeQuery(id+"F0.imprint","IMPRINT",FACE,{"disambiguationData":[TD([[makeQuery(id+"F0.imprint","IMPRINT",EDGE,{"disambiguationData":[TD([[subQ2,1.0]])],"derivedFrom":subQ1}),1.0]])]});}
            extrude(context, id + "F2", {"entities" : qUnion([Q0, Q1, Q2, Q3, Q4, Q5, Q6, Q7, Q8]), "operationType" : NewBodyOperationType.ADD, "depth" : 220 * mm, "offsetDistance" : 25 * mm});
        }
        {
            var Q0;
            {var subQ5=sQuery(id+"F0.wireOp",EDGE,"G2edZedI-oMVv-zGGG-3rpf-8qc5Rzpi7jZh.bottom");Q0=makeQuery(id+"F0.imprint","IMPRINT",FACE,{"disambiguationData":[TD([[makeQuery(id+"F0.imprint","IMPRINT",EDGE,{"derivedFrom":subQ5}),1.0]])]});}
            var Q1;
            {var subQ0=sQuery(id+"F0.wireOp",EDGE,"G2edZedI-oMVv-zGGG-3rpf-8qc5Rzpi7jZh.left");var subQ1=sQuery(id+"F0.wireOp",EDGE,"MHhcaKt2-idaq-ussF-yxv1-Ysw6X7YejIML.top");var subQ2=makeQuery(id+"F0.imprint","INTERSECT",VERTEX,{"derivedFrom":[subQ1,subQ0]});Q1=makeQuery(id+"F0.imprint","IMPRINT",FACE,{"disambiguationData":[TD([[makeQuery(id+"F0.imprint","IMPRINT",EDGE,{"disambiguationData":[TD([[subQ2,-1.0]])],"derivedFrom":subQ1}),-1.0]])]});}
            var Q2;
            {var subQ0=sQuery(id+"F0.wireOp",EDGE,"G2edZedI-oMVv-zGGG-3rpf-8qc5Rzpi7jZh.left");var subQ1=sQuery(id+"F0.wireOp",EDGE,"MHhcaKt2-idaq-ussF-yxv1-Ysw6X7YejIML.top");var subQ2=makeQuery(id+"F0.imprint","INTERSECT",VERTEX,{"derivedFrom":[subQ1,subQ0]});Q2=makeQuery(id+"F0.imprint","IMPRINT",FACE,{"disambiguationData":[TD([[makeQuery(id+"F0.imprint","IMPRINT",EDGE,{"disambiguationData":[TD([[subQ2,-1.0]])],"derivedFrom":subQ1}),1.0]])]});}
            var Q3;
            {var subQ0=sQuery(id+"F0.wireOp",EDGE,"G2edZedI-oMVv-zGGG-3rpf-8qc5Rzpi7jZh.left");var subQ1=sQuery(id+"F0.wireOp",EDGE,"UooLEnTI-Uf4f-MH2r-6JwD-Mf36DO2BtYOc.bottom");var subQ2=makeQuery(id+"F0.imprint","INTERSECT",VERTEX,{"derivedFrom":[subQ1,subQ0]});Q3=makeQuery(id+"F0.imprint","IMPRINT",FACE,{"disambiguationData":[TD([[makeQuery(id+"F0.imprint","IMPRINT",EDGE,{"disambiguationData":[TD([[subQ2,-1.0]])],"derivedFrom":subQ1}),1.0]])]});}
            var Q4;
            {var subQ0=sQuery(id+"F0.wireOp",EDGE,"G2edZedI-oMVv-zGGG-3rpf-8qc5Rzpi7jZh.left");var subQ1=sQuery(id+"F0.wireOp",EDGE,"MHhcaKt2-idaq-ussF-yxv1-Ysw6X7YejIML.bottom");var subQ2=makeQuery(id+"F0.imprint","INTERSECT",VERTEX,{"derivedFrom":[subQ1,subQ0]});Q4=makeQuery(id+"F0.imprint","IMPRINT",FACE,{"disambiguationData":[TD([[makeQuery(id+"F0.imprint","IMPRINT",EDGE,{"disambiguationData":[TD([[subQ2,-1.0]])],"derivedFrom":subQ1}),-1.0]])]});}
            var Q5;
            {var subQ0=sQuery(id+"F0.wireOp",EDGE,"G2edZedI-oMVv-zGGG-3rpf-8qc5Rzpi7jZh.left");var subQ1=sQuery(id+"F0.wireOp",EDGE,"MHhcaKt2-idaq-ussF-yxv1-Ysw6X7YejIML.bottom");var subQ2=makeQuery(id+"F0.imprint","INTERSECT",VERTEX,{"derivedFrom":[subQ1,subQ0]});Q5=makeQuery(id+"F0.imprint","IMPRINT",FACE,{"disambiguationData":[TD([[makeQuery(id+"F0.imprint","IMPRINT",EDGE,{"disambiguationData":[TD([[subQ2,-1.0]])],"derivedFrom":subQ1}),1.0]])]});}
            var Q6;
            {var subQ5=sQuery(id+"F0.wireOp",EDGE,"G2edZedI-oMVv-zGGG-3rpf-8qc5Rzpi7jZh.top");Q6=makeQuery(id+"F0.imprint","IMPRINT",FACE,{"disambiguationData":[TD([[makeQuery(id+"F0.imprint","IMPRINT",EDGE,{"derivedFrom":subQ5}),-1.0]])]});}
            var Q7;
            {var subQ5=sQuery(id+"F0.wireOp",EDGE,"UooLEnTI-Uf4f-MH2r-6JwD-Mf36DO2BtYOc.left");Q7=makeQuery(id+"F0.imprint","IMPRINT",FACE,{"disambiguationData":[TD([[makeQuery(id+"F0.imprint","IMPRINT",EDGE,{"derivedFrom":subQ5}),-1.0]])]});}
            var Q8;
            {var subQ5=sQuery(id+"F0.wireOp",EDGE,"UooLEnTI-Uf4f-MH2r-6JwD-Mf36DO2BtYOc.right");Q8=makeQuery(id+"F0.imprint","IMPRINT",FACE,{"disambiguationData":[TD([[makeQuery(id+"F0.imprint","IMPRINT",EDGE,{"derivedFrom":subQ5}),1.0]])]});}
            var Q9;
            {var subQ0=sQuery(id+"F0.wireOp",EDGE,"03e8Ckts-ZFi5-Aq3V-xVUe-yBUDc2XyNOQ6");Q9=makeQuery(id+"F0.imprint","IMPRINT",FACE,{"disambiguationData":[TD([[makeQuery(id+"F0.imprint","IMPRINT",EDGE,{"derivedFrom":subQ0}),1.0]])]});}
            var Q10;
            {var subQ0=sQuery(id+"F0.wireOp",EDGE,"bj91yUHZ-Wt7Y-C2vt-p8Xj-VTrvMNZv7KkJ");Q10=makeQuery(id+"F0.imprint","IMPRINT",FACE,{"disambiguationData":[TD([[makeQuery(id+"F0.imprint","IMPRINT",EDGE,{"derivedFrom":subQ0}),-1.0]])]});}
            var Q11;
            {var subQ0=sQuery(id+"F0.wireOp",EDGE,"UsHAKyTv-6jtb-spoe-rsad-w7DXaWFApGhJ");Q11=makeQuery(id+"F0.imprint","IMPRINT",FACE,{"disambiguationData":[TD([[makeQuery(id+"F0.imprint","IMPRINT",EDGE,{"derivedFrom":subQ0}),1.0]])]});}
            var Q12;
            {var subQ5=sQuery(id+"F0.wireOp",EDGE,"U6Gb84Ca-BoU4-zACI-EIev-EI8B9hxLx2hd.bottom");Q12=makeQuery(id+"F0.imprint","IMPRINT",FACE,{"disambiguationData":[TD([[makeQuery(id+"F0.imprint","IMPRINT",EDGE,{"derivedFrom":subQ5}),-1.0]])]});}
            var Q13;
            {var subQ5=sQuery(id+"F0.wireOp",EDGE,"KJFaWd3U-YvpL-C540-iaLV-ns6R3owsW4g9.left");Q13=makeQuery(id+"F0.imprint","IMPRINT",FACE,{"disambiguationData":[TD([[makeQuery(id+"F0.imprint","IMPRINT",EDGE,{"derivedFrom":subQ5}),1.0]])]});}
            var Q14;
            {var subQ5=sQuery(id+"F0.wireOp",EDGE,"WVTM5ykO-ORzQ-6imj-rCBD-ZudhNr8kMxeS.bottom");Q14=makeQuery(id+"F0.imprint","IMPRINT",FACE,{"disambiguationData":[TD([[makeQuery(id+"F0.imprint","IMPRINT",EDGE,{"derivedFrom":subQ5}),1.0]])]});}
            var Q15;
            {var subQ5=sQuery(id+"F0.wireOp",EDGE,"YnwhtgPZ-tjwQ-rwOe-Yv9D-G0hxzTefPX9C.left");Q15=makeQuery(id+"F0.imprint","IMPRINT",FACE,{"disambiguationData":[TD([[makeQuery(id+"F0.imprint","IMPRINT",EDGE,{"derivedFrom":subQ5}),-1.0]])]});}
            var Q16;
            {var subQ0=sQuery(id+"F0.wireOp",EDGE,"3ec345ef-f0f0-4e93-9e5e-b6a35eb55933.1.15");var subQ1=sQuery(id+"F0.wireOp",EDGE,"G2edZedI-oMVv-zGGG-3rpf-8qc5Rzpi7jZh.right");var subQ2=makeQuery(id+"F0.imprint","INTERSECT",VERTEX,{"derivedFrom":[subQ1,subQ0]});Q16=makeQuery(id+"F0.imprint","IMPRINT",FACE,{"disambiguationData":[TD([[makeQuery(id+"F0.imprint","IMPRINT",EDGE,{"disambiguationData":[TD([[subQ2,-1.0]])],"derivedFrom":subQ1}),1.0]])]});}
            var Q17;
            {var subQ0=sQuery(id+"F0.wireOp",EDGE,"Fhyrr48q-6Ub6-qUJE-WvSH-lKAYv9wGpefs");var subQ1=sQuery(id+"F0.wireOp",EDGE,"G2edZedI-oMVv-zGGG-3rpf-8qc5Rzpi7jZh.right");var subQ2=makeQuery(id+"F0.imprint","INTERSECT",VERTEX,{"derivedFrom":[subQ1,subQ0]});Q17=makeQuery(id+"F0.imprint","IMPRINT",FACE,{"disambiguationData":[TD([[makeQuery(id+"F0.imprint","IMPRINT",EDGE,{"disambiguationData":[TD([[subQ2,1.0]])],"derivedFrom":subQ1}),1.0]])]});}
            var Q18;
            {var subQ0=sQuery(id+"F0.wireOp",EDGE,"Fhyrr48q-6Ub6-qUJE-WvSH-lKAYv9wGpefs");var subQ1=sQuery(id+"F0.wireOp",EDGE,"G2edZedI-oMVv-zGGG-3rpf-8qc5Rzpi7jZh.right");var subQ2=makeQuery(id+"F0.imprint","INTERSECT",VERTEX,{"derivedFrom":[subQ1,subQ0]});Q18=makeQuery(id+"F0.imprint","IMPRINT",FACE,{"disambiguationData":[TD([[makeQuery(id+"F0.imprint","IMPRINT",EDGE,{"disambiguationData":[TD([[subQ2,1.0]])],"derivedFrom":subQ1}),-1.0]])]});}
            var Q19;
            {var subQ0=sQuery(id+"F0.wireOp",EDGE,"Fhyrr48q-6Ub6-qUJE-WvSH-lKAYv9wGpefs");var subQ1=sQuery(id+"F0.wireOp",EDGE,"G2edZedI-oMVv-zGGG-3rpf-8qc5Rzpi7jZh.left");var subQ2=makeQuery(id+"F0.imprint","INTERSECT",VERTEX,{"derivedFrom":[subQ1,subQ0]});Q19=makeQuery(id+"F0.imprint","IMPRINT",FACE,{"disambiguationData":[TD([[makeQuery(id+"F0.imprint","IMPRINT",EDGE,{"disambiguationData":[TD([[subQ2,1.0]])],"derivedFrom":subQ1}),-1.0]])]});}
            var Q20;
            {var subQ0=sQuery(id+"F0.wireOp",EDGE,"3ec345ef-f0f0-4e93-9e5e-b6a35eb55933.2.15");var subQ1=sQuery(id+"F0.wireOp",EDGE,"G2edZedI-oMVv-zGGG-3rpf-8qc5Rzpi7jZh.left");var subQ2=makeQuery(id+"F0.imprint","INTERSECT",VERTEX,{"derivedFrom":[subQ1,subQ0]});Q20=makeQuery(id+"F0.imprint","IMPRINT",FACE,{"disambiguationData":[TD([[makeQuery(id+"F0.imprint","IMPRINT",EDGE,{"disambiguationData":[TD([[subQ2,-1.0]])],"derivedFrom":subQ1}),-1.0]])]});}
            var Q21;
            {var subQ0=sQuery(id+"F0.wireOp",EDGE,"Fhyrr48q-6Ub6-qUJE-WvSH-lKAYv9wGpefs");var subQ1=sQuery(id+"F0.wireOp",EDGE,"G2edZedI-oMVv-zGGG-3rpf-8qc5Rzpi7jZh.left");var subQ2=makeQuery(id+"F0.imprint","INTERSECT",VERTEX,{"derivedFrom":[subQ1,subQ0]});Q21=makeQuery(id+"F0.imprint","IMPRINT",FACE,{"disambiguationData":[TD([[makeQuery(id+"F0.imprint","IMPRINT",EDGE,{"disambiguationData":[TD([[subQ2,1.0]])],"derivedFrom":subQ1}),1.0]])]});}
            var Q22;
            {var subQ0=sQuery(id+"F0.wireOp",EDGE,"3ec345ef-f0f0-4e93-9e5e-b6a35eb55933.1.15");var subQ1=sQuery(id+"F0.wireOp",EDGE,"3ec345ef-f0f0-4e93-9e5e-b6a35eb55933.1.2");var subQ2=makeQuery(id+"F0.imprint","INTERSECT",VERTEX,{"derivedFrom":[subQ1,subQ0]});Q22=makeQuery(id+"F0.imprint","IMPRINT",FACE,{"disambiguationData":[TD([[makeQuery(id+"F0.imprint","IMPRINT",EDGE,{"disambiguationData":[TD([[subQ2,1.0]])],"derivedFrom":subQ1}),-1.0]])]});}
            var Q23;
            {var subQ0=sQuery(id+"F0.wireOp",EDGE,"3ec345ef-f0f0-4e93-9e5e-b6a35eb55933.1.15");var subQ1=sQuery(id+"F0.wireOp",EDGE,"3ec345ef-f0f0-4e93-9e5e-b6a35eb55933.1.2");var subQ2=makeQuery(id+"F0.imprint","INTERSECT",VERTEX,{"derivedFrom":[subQ1,subQ0]});Q23=makeQuery(id+"F0.imprint","IMPRINT",FACE,{"disambiguationData":[TD([[makeQuery(id+"F0.imprint","IMPRINT",EDGE,{"disambiguationData":[TD([[subQ2,1.0]])],"derivedFrom":subQ1}),1.0]])]});}
            var Q24;
            {var subQ0=sQuery(id+"F0.wireOp",EDGE,"3ec345ef-f0f0-4e93-9e5e-b6a35eb55933.2.15");var subQ1=sQuery(id+"F0.wireOp",EDGE,"3ec345ef-f0f0-4e93-9e5e-b6a35eb55933.1.2");var subQ2=makeQuery(id+"F0.imprint","INTERSECT",VERTEX,{"derivedFrom":[subQ1,subQ0]});Q24=makeQuery(id+"F0.imprint","IMPRINT",FACE,{"disambiguationData":[TD([[makeQuery(id+"F0.imprint","IMPRINT",EDGE,{"disambiguationData":[TD([[subQ2,-1.0]])],"derivedFrom":subQ1}),1.0]])]});}
            var Q25;
            {var subQ5=sQuery(id+"F0.wireOp",EDGE,"3ec345ef-f0f0-4e93-9e5e-b6a35eb55933.1.17");Q25=makeQuery(id+"F0.imprint","IMPRINT",FACE,{"disambiguationData":[TD([[makeQuery(id+"F0.imprint","IMPRINT",EDGE,{"derivedFrom":subQ5}),1.0]])]});}
            var Q26;
            {var subQ5=sQuery(id+"F0.wireOp",EDGE,"3ec345ef-f0f0-4e93-9e5e-b6a35eb55933.2.17");Q26=makeQuery(id+"F0.imprint","IMPRINT",FACE,{"disambiguationData":[TD([[makeQuery(id+"F0.imprint","IMPRINT",EDGE,{"derivedFrom":subQ5}),1.0]])]});}
            var Q27;
            {var subQ0=sQuery(id+"F0.wireOp",EDGE,"U6Gb84Ca-BoU4-zACI-EIev-EI8B9hxLx2hd.bottom");Q27=makeQuery(id+"F0.imprint","IMPRINT",FACE,{"disambiguationData":[TD([[makeQuery(id+"F0.imprint","IMPRINT",EDGE,{"derivedFrom":subQ0}),1.0]])]});}
            var Q28;
            {var subQ0=sQuery(id+"F0.wireOp",EDGE,"U6Gb84Ca-BoU4-zACI-EIev-EI8B9hxLx2hd.top");Q28=makeQuery(id+"F0.imprint","IMPRINT",FACE,{"disambiguationData":[TD([[makeQuery(id+"F0.imprint","IMPRINT",EDGE,{"derivedFrom":subQ0}),-1.0]])]});}
            var Q29;
            {var subQ3=sQuery(id+"F0.wireOp",EDGE,"3ec345ef-f0f0-4e93-9e5e-b6a35eb55933.1.11");Q29=makeQuery(id+"F0.imprint","IMPRINT",FACE,{"disambiguationData":[TD([[makeQuery(id+"F0.imprint","IMPRINT",EDGE,{"derivedFrom":subQ3}),-1.0]])]});}
            var Q30;
            {var subQ2=sQuery(id+"F0.wireOp",EDGE,"3ec345ef-f0f0-4e93-9e5e-b6a35eb55933.1.11");Q30=makeQuery(id+"F0.imprint","IMPRINT",FACE,{"disambiguationData":[TD([[makeQuery(id+"F0.imprint","IMPRINT",EDGE,{"derivedFrom":subQ2}),1.0]])]});}
            var Q31;
            {var subQ3=sQuery(id+"F0.wireOp",EDGE,"3ec345ef-f0f0-4e93-9e5e-b6a35eb55933.2.11");Q31=makeQuery(id+"F0.imprint","IMPRINT",FACE,{"disambiguationData":[TD([[makeQuery(id+"F0.imprint","IMPRINT",EDGE,{"derivedFrom":subQ3}),-1.0]])]});}
            var Q32;
            {var subQ2=sQuery(id+"F0.wireOp",EDGE,"3ec345ef-f0f0-4e93-9e5e-b6a35eb55933.2.11");Q32=makeQuery(id+"F0.imprint","IMPRINT",FACE,{"disambiguationData":[TD([[makeQuery(id+"F0.imprint","IMPRINT",EDGE,{"derivedFrom":subQ2}),1.0]])]});}
            var Q33;
            {var subQ3=sQuery(id+"F0.wireOp",EDGE,"E2");var subQ13=sQuery(id+"F0.wireOp",EDGE,"E7");var subQ14=makeQuery(id+"F0.imprint","INTERSECT",VERTEX,{"derivedFrom":[subQ3,subQ13]});Q33=makeQuery(id+"F0.imprint","IMPRINT",FACE,{"disambiguationData":[TD([[makeQuery(id+"F0.imprint","IMPRINT",EDGE,{"disambiguationData":[TD([[subQ14,-1.0]])],"derivedFrom":subQ3}),1.0]])]});}
            var Q34;
            {var subQ0=sQuery(id+"F0.wireOp",EDGE,"E7");var subQ1=sQuery(id+"F0.wireOp",EDGE,"E2");var subQ2=makeQuery(id+"F0.imprint","INTERSECT",VERTEX,{"derivedFrom":[subQ1,subQ0]});Q34=makeQuery(id+"F0.imprint","IMPRINT",FACE,{"disambiguationData":[TD([[makeQuery(id+"F0.imprint","IMPRINT",EDGE,{"disambiguationData":[TD([[subQ2,-1.0]])],"derivedFrom":subQ1}),-1.0]])]});}
            var Q35;
            {var subQ0=sQuery(id+"F0.wireOp",EDGE,"E18.1.1");var subQ1=sQuery(id+"F0.wireOp",EDGE,"E2");var subQ2=makeQuery(id+"F0.imprint","INTERSECT",VERTEX,{"derivedFrom":[subQ1,subQ0]});Q35=makeQuery(id+"F0.imprint","IMPRINT",FACE,{"disambiguationData":[TD([[makeQuery(id+"F0.imprint","IMPRINT",EDGE,{"disambiguationData":[TD([[subQ2,-1.0]])],"derivedFrom":subQ1}),-1.0]])]});}
            var Q36;
            {var subQ0=sQuery(id+"F0.wireOp",EDGE,"E18.2.1");var subQ1=sQuery(id+"F0.wireOp",EDGE,"E2");var subQ2=makeQuery(id+"F0.imprint","INTERSECT",VERTEX,{"derivedFrom":[subQ1,subQ0]});Q36=makeQuery(id+"F0.imprint","IMPRINT",FACE,{"disambiguationData":[TD([[makeQuery(id+"F0.imprint","IMPRINT",EDGE,{"disambiguationData":[TD([[subQ2,-1.0]])],"derivedFrom":subQ1}),-1.0]])]});}
            extrude(context, id + "F3", {"entities" : qUnion([Q0, Q1, Q2, Q3, Q4, Q5, Q6, Q7, Q8, Q9, Q10, Q11, Q12, Q13, Q14, Q15, Q16, Q17, Q18, Q19, Q20, Q21, Q22, Q23, Q24, Q25, Q26, Q27, Q28, Q29, Q30, Q31, Q32, Q33, Q34, Q35, Q36]), "operationType" : NewBodyOperationType.ADD, "depth" : 235 * mm, "offsetDistance" : 25 * mm});
        }
        {
            var Q0;
            Q0=makeQuery(id+"F3.opExtrude","CAP_EDGE",EDGE,{"disambiguationData":[OSD([sQuery(id+"F0.wireOp",EDGE,"E18.2.8")])],"isStart":false});
            var Q1;
            Q1=makeQuery(id+"F3.opExtrude","CAP_EDGE",EDGE,{"disambiguationData":[OSD([sQuery(id+"F0.wireOp",EDGE,"E18.1.8")])],"isStart":false});
            var Q2;
            Q2=makeQuery(id+"F3.opExtrude","CAP_EDGE",EDGE,{"disambiguationData":[OSD([sQuery(id+"F0.wireOp",EDGE,"E17")])],"isStart":false});
            chamfer(context, id + "F4", {"entities" : qUnion([Q0, Q1, Q2]), "chamferType" : ChamferType.OFFSET_ANGLE, "width" : 15 * mm, "oppositeDirection" : false, "angle" : 75 * degree, "tangentPropagation" : true});
        }
        {
            var Q0;
            {var subQ0=sQuery(id+"F0.wireOp",EDGE,"ARnEnpE5-tkmW-Q9Fp-N7HQ-ZdpaRJQSmeqH.bottom");var subQ1=sQuery(id+"F0.wireOp",EDGE,"E1");Q0=makeQuery(id+"F2.opExtrude","CAP_EDGE",EDGE,{"disambiguationData":[OSD([subQ1]),TDD([makeQuery(id+"F0.imprint","IMPRINT",EDGE,{"disambiguationData":[TD([[makeQuery(id+"F0.imprint","INTERSECT",VERTEX,{"derivedFrom":[subQ1,subQ0,sQuery(id+"F0.wireOp",EDGE,"ARnEnpE5-tkmW-Q9Fp-N7HQ-ZdpaRJQSmeqH.left"),sQuery(id+"F0.wireOp",EDGE,"UsHAKyTv-6jtb-spoe-rsad-w7DXaWFApGhJ")]}),-1.0]])],"derivedFrom":subQ1})])],"isStart":false});}
            var Q1;
            {var subQ0=sQuery(id+"F0.wireOp",EDGE,"fYTYB3PY-5dvC-i0FG-IhBz-imLdNv0oFj73.left");var subQ1=sQuery(id+"F0.wireOp",EDGE,"E1");Q1=makeQuery(id+"F2.opExtrude","CAP_EDGE",EDGE,{"disambiguationData":[OSD([subQ1]),TDD([makeQuery(id+"F0.imprint","IMPRINT",EDGE,{"disambiguationData":[TD([[makeQuery(id+"F0.imprint","INTERSECT",VERTEX,{"derivedFrom":[subQ1,sQuery(id+"F0.wireOp",EDGE,"fYTYB3PY-5dvC-i0FG-IhBz-imLdNv0oFj73.bottom"),subQ0,sQuery(id+"F0.wireOp",EDGE,"kZxKVhXT-tHgl-xRPm-lkcx-u0khmLZUqcnL")]}),1.0]])],"derivedFrom":subQ1})])],"isStart":false});}
            var Q2;
            {var subQ0=sQuery(id+"F0.wireOp",EDGE,"JRACFuVa-LFQl-MoOF-o5kD-FoGYgOgg0vGQ.bottom");var subQ1=sQuery(id+"F0.wireOp",EDGE,"E1");Q2=makeQuery(id+"F2.opExtrude","CAP_EDGE",EDGE,{"disambiguationData":[OSD([subQ1]),TDD([makeQuery(id+"F0.imprint","IMPRINT",EDGE,{"disambiguationData":[TD([[makeQuery(id+"F0.imprint","INTERSECT",VERTEX,{"derivedFrom":[subQ1,subQ0,sQuery(id+"F0.wireOp",EDGE,"JRACFuVa-LFQl-MoOF-o5kD-FoGYgOgg0vGQ.left"),sQuery(id+"F0.wireOp",EDGE,"CjHSthgf-UrMd-mykl-wSX2-3saethCeIdIi")]}),1.0]])],"derivedFrom":subQ1})])],"isStart":false});}
            var Q3;
            {var subQ0=sQuery(id+"F0.wireOp",EDGE,"qvxIDn41-u5vC-3tcf-A1ba-gfAf9TCSAjBw.left");var subQ1=sQuery(id+"F0.wireOp",EDGE,"E1");Q3=makeQuery(id+"F2.opExtrude","CAP_EDGE",EDGE,{"disambiguationData":[OSD([subQ1]),TDD([makeQuery(id+"F0.imprint","IMPRINT",EDGE,{"disambiguationData":[TD([[makeQuery(id+"F0.imprint","INTERSECT",VERTEX,{"derivedFrom":[subQ1,sQuery(id+"F0.wireOp",EDGE,"qvxIDn41-u5vC-3tcf-A1ba-gfAf9TCSAjBw.bottom"),subQ0,sQuery(id+"F0.wireOp",EDGE,"A8od2ZFF-7y6o-rShD-bBN7-uJ0yuPEPxqf4")]}),-1.0]])],"derivedFrom":subQ1})])],"isStart":false});}
            var Q4;
            {var subQ0=sQuery(id+"F0.wireOp",EDGE,"E1");Q4=makeQuery(id+"F3.opExtrude","CAP_EDGE",EDGE,{"disambiguationData":[OSD([subQ0]),TDD([makeQuery(id+"F0.imprint","IMPRINT",EDGE,{"disambiguationData":[TD([[makeQuery(id+"F0.imprint","INTERSECT",VERTEX,{"derivedFrom":[subQ0,sQuery(id+"F0.wireOp",EDGE,"E18.1.0")]}),1.0]])],"derivedFrom":subQ0})])],"isStart":false});}
            var Q5;
            {var subQ0=sQuery(id+"F0.wireOp",EDGE,"E1");Q5=makeQuery(id+"F3.opExtrude","CAP_EDGE",EDGE,{"disambiguationData":[OSD([subQ0]),TDD([makeQuery(id+"F0.imprint","IMPRINT",EDGE,{"disambiguationData":[TD([[makeQuery(id+"F0.imprint","INTERSECT",VERTEX,{"derivedFrom":[subQ0,sQuery(id+"F0.wireOp",EDGE,"E18.2.0")]}),1.0]])],"derivedFrom":subQ0})])],"isStart":false});}
            var Q6;
            {var subQ0=sQuery(id+"F0.wireOp",EDGE,"E1");Q6=makeQuery(id+"F3.opExtrude","CAP_EDGE",EDGE,{"disambiguationData":[OSD([subQ0]),TDD([makeQuery(id+"F0.imprint","IMPRINT",EDGE,{"disambiguationData":[TD([[makeQuery(id+"F0.imprint","INTERSECT",VERTEX,{"derivedFrom":[subQ0,sQuery(id+"F0.wireOp",EDGE,"E6")]}),1.0]])],"derivedFrom":subQ0})])],"isStart":false});}
            fillet(context, id + "F5", {"entities" : qUnion([Q0, Q1, Q2, Q3, Q4, Q5, Q6]), "radius" : 6 * mm, "tangentPropagation" : true, "allowEdgeOverflow" : false});
        }
        {
            var Q0;
            Q0=makeQuery(id+"F0.imprint","IMPRINT",FACE,{"disambiguationData":[TD([[makeQuery(id+"F0.imprint","IMPRINT",EDGE,{"derivedFrom":sQuery(id+"F0.wireOp",EDGE,"E11")}),1.0]])]});
            var Q1;
            Q1=makeQuery(id+"F0.imprint","IMPRINT",FACE,{"disambiguationData":[TD([[makeQuery(id+"F0.imprint","IMPRINT",EDGE,{"derivedFrom":sQuery(id+"F0.wireOp",EDGE,"E13.1.0")}),-1.0]])]});
            var Q2;
            Q2=makeQuery(id+"F0.imprint","IMPRINT",FACE,{"disambiguationData":[TD([[makeQuery(id+"F0.imprint","IMPRINT",EDGE,{"derivedFrom":sQuery(id+"F0.wireOp",EDGE,"E13.2.0")}),-1.0]])]});
            extrude(context, id + "F6", {"entities" : qUnion([Q0, Q1, Q2]), "operationType" : NewBodyOperationType.ADD, "depth" : 3 * mm, "offsetDistance" : 25 * mm});
        }
        {
            var Q0;
            {var subQ4=sQuery(id+"F0.wireOp",EDGE,"E18.1.4");Q0=makeQuery(id+"F0.imprint","IMPRINT",FACE,{"disambiguationData":[TD([[makeQuery(id+"F0.imprint","IMPRINT",EDGE,{"derivedFrom":subQ4}),1.0]])]});}
            var Q1;
            {var subQ2=sQuery(id+"F0.wireOp",EDGE,"E18.2.4");Q1=makeQuery(id+"F0.imprint","IMPRINT",FACE,{"disambiguationData":[TD([[makeQuery(id+"F0.imprint","IMPRINT",EDGE,{"derivedFrom":subQ2}),1.0]])]});}
            var Q2;
            {var subQ2=sQuery(id+"F0.wireOp",EDGE,"E8");Q2=makeQuery(id+"F0.imprint","IMPRINT",FACE,{"disambiguationData":[TD([[makeQuery(id+"F0.imprint","IMPRINT",EDGE,{"derivedFrom":subQ2}),1.0]])]});}
            extrude(context, id + "F7", {"entities" : qUnion([Q0, Q1, Q2]), "operationType" : NewBodyOperationType.ADD, "depth" : 30 * mm, "offsetDistance" : 25 * mm});
        }
        {
            var Q0;
            Q0=qCreatedBy(makeId("Top.planeOp"),FACE);
            var sketch = newSketch(context, id + "F8", { "sketchPlane" : qUnion([Q0])});
            skLineSegment(sketch, "E20.bottom", {"start": v(100, 100) * mm, "end": v(-100, 100) * mm});
            skLineSegment(sketch, "E20.top", {"start": v(100, -100) * mm, "end": v(-100, -100) * mm});
            skLineSegment(sketch, "E20.left", {"start": v(100, 100) * mm, "end": v(100, -100) * mm});
            skLineSegment(sketch, "E20.right", {"start": v(-100, 100) * mm, "end": v(-100, -100) * mm});
            skPoint(sketch, "E20.middle", {"position": v(0, 0) * mm});
            skSolve(sketch);
        }
        {
            var Q0;
            Q0=makeQuery(id+"F8.imprint","IMPRINT",FACE,{"disambiguationData":[TD([[makeQuery(id+"F8.imprint","IMPRINT",EDGE,{"derivedFrom":sQuery(id+"F8.wireOp",EDGE,"E20.bottom")}),1.0]])]});
            extrude(context, id + "F9", {"entities" : qUnion([Q0]), "operationType" : NewBodyOperationType.ADD, "oppositeDirection" : true, "depth" : 20 * mm, "offsetDistance" : 25 * mm});
        }
        {
            var Q0;
            Q0=makeQuery(id+"F9.opExtrude","SWEPT_EDGE",EDGE,{"disambiguationData":[OSD([sQuery(id+"F8.wireOp",EDGE,"E20.top"),sQuery(id+"F8.wireOp",EDGE,"E20.right")])]});
            var Q1;
            Q1=makeQuery(id+"F9.opExtrude","SWEPT_EDGE",EDGE,{"disambiguationData":[OSD([sQuery(id+"F8.wireOp",EDGE,"E20.top"),sQuery(id+"F8.wireOp",EDGE,"E20.left")])]});
            var Q2;
            Q2=makeQuery(id+"F9.opExtrude","SWEPT_EDGE",EDGE,{"disambiguationData":[OSD([sQuery(id+"F8.wireOp",EDGE,"E20.bottom"),sQuery(id+"F8.wireOp",EDGE,"E20.left")])]});
            var Q3;
            Q3=makeQuery(id+"F9.opExtrude","SWEPT_EDGE",EDGE,{"disambiguationData":[OSD([sQuery(id+"F8.wireOp",EDGE,"E20.bottom"),sQuery(id+"F8.wireOp",EDGE,"E20.right")])]});
            fillet(context, id + "F10", {"entities" : qUnion([Q0, Q1, Q2, Q3]), "radius" : 5 * mm, "tangentPropagation" : true, "allowEdgeOverflow" : false});
        }
        {
            var Q0;
            Q0=makeQuery(id+"F0.imprint","IMPRINT",FACE,{"disambiguationData":[TD([[makeQuery(id+"F0.imprint","IMPRINT",EDGE,{"derivedFrom":sQuery(id+"F0.wireOp",EDGE,"E19.sketch_text.stroke-0")}),-1.0]])]});
            var Q1;
            Q1=makeQuery(id+"F0.imprint","IMPRINT",FACE,{"disambiguationData":[TD([[makeQuery(id+"F0.imprint","IMPRINT",EDGE,{"derivedFrom":sQuery(id+"F0.wireOp",EDGE,"E19.sketch_text.stroke-6")}),-1.0]])]});
            var Q2;
            Q2=makeQuery(id+"F0.imprint","IMPRINT",FACE,{"disambiguationData":[TD([[makeQuery(id+"F0.imprint","IMPRINT",EDGE,{"derivedFrom":sQuery(id+"F0.wireOp",EDGE,"E19.sketch_text.stroke-26")}),-1.0]])]});
            var Q3;
            Q3=makeQuery(id+"F0.imprint","IMPRINT",FACE,{"disambiguationData":[TD([[makeQuery(id+"F0.imprint","IMPRINT",EDGE,{"derivedFrom":sQuery(id+"F0.wireOp",EDGE,"E19.sketch_text.stroke-51")}),-1.0]])]});
            var Q4;
            Q4=makeQuery(id+"F0.imprint","IMPRINT",FACE,{"disambiguationData":[TD([[makeQuery(id+"F0.imprint","IMPRINT",EDGE,{"derivedFrom":sQuery(id+"F0.wireOp",EDGE,"E19.sketch_text.stroke-67")}),-1.0]])]});
            var Q5;
            Q5=makeQuery(id+"F0.imprint","IMPRINT",FACE,{"disambiguationData":[TD([[makeQuery(id+"F0.imprint","IMPRINT",EDGE,{"derivedFrom":sQuery(id+"F0.wireOp",EDGE,"E19.sketch_text.stroke-79")}),-1.0]])]});
            var Q6;
            Q6=makeQuery(id+"F0.imprint","IMPRINT",FACE,{"disambiguationData":[TD([[makeQuery(id+"F0.imprint","IMPRINT",EDGE,{"derivedFrom":sQuery(id+"F0.wireOp",EDGE,"E19.sketch_text.stroke-99")}),-1.0]])]});
            var Q7;
            Q7=makeQuery(id+"F0.imprint","IMPRINT",FACE,{"disambiguationData":[TD([[makeQuery(id+"F0.imprint","IMPRINT",EDGE,{"derivedFrom":sQuery(id+"F0.wireOp",EDGE,"E19.sketch_text.stroke-125")}),-1.0]])]});
            extrude(context, id + "F11", {"entities" : qUnion([Q0, Q1, Q2, Q3, Q4, Q5, Q6, Q7]), "operationType" : NewBodyOperationType.ADD, "depth" : 1 * mm, "offsetDistance" : 25 * mm});
        }
    });
